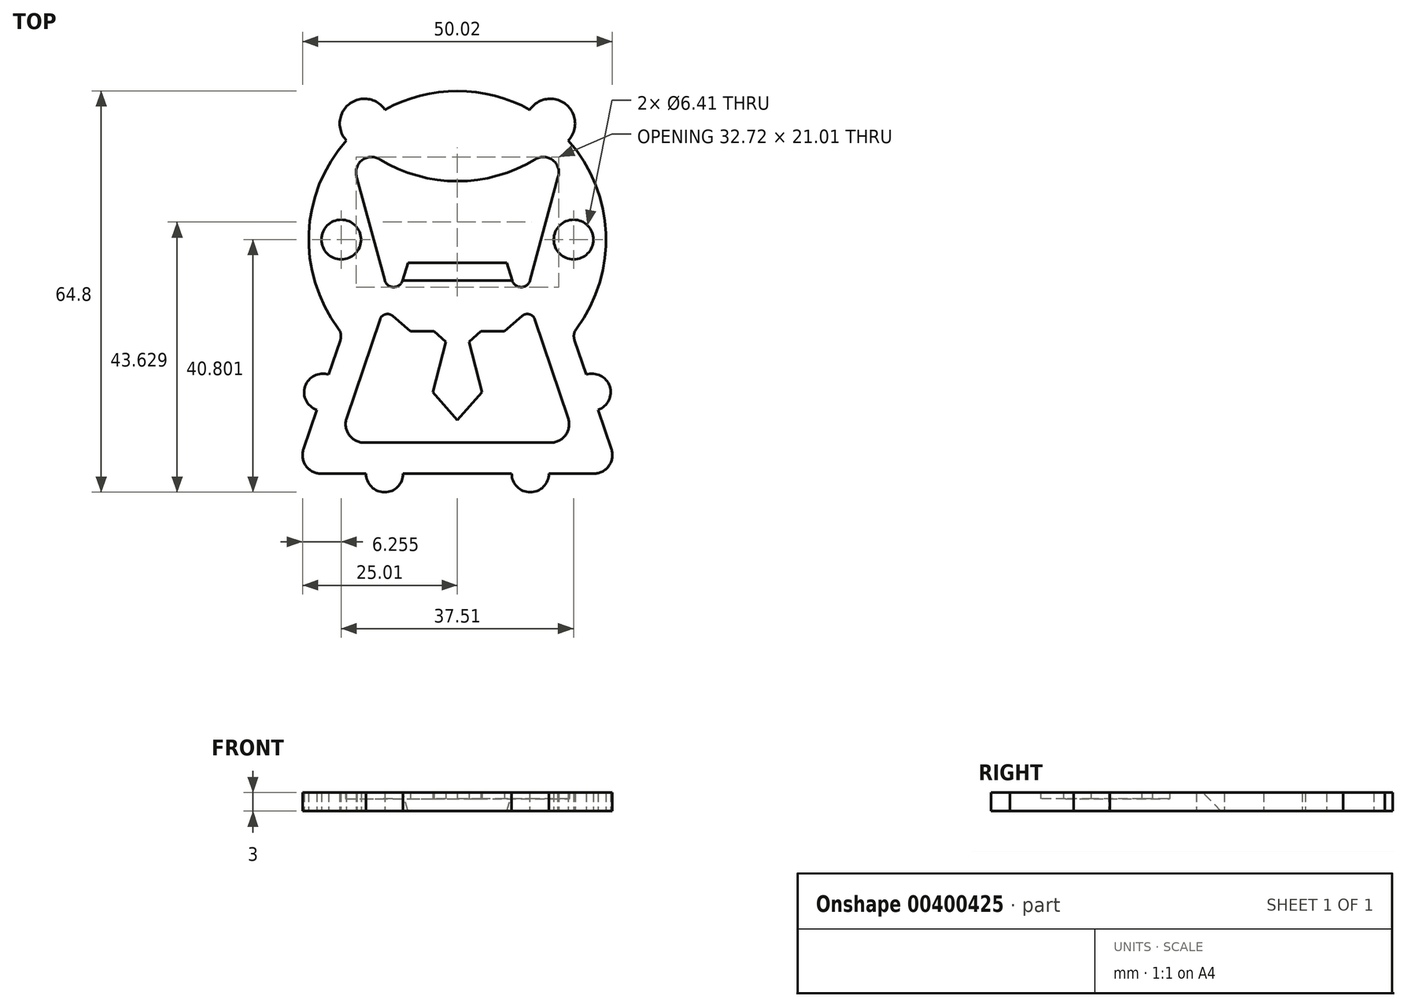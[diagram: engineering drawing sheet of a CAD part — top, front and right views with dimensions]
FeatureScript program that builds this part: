
annotation { "Feature Type Name" : "Feature", "Feature Type Description" : "" }
export const myFeature = defineFeature(function(context is Context, id is Id, definition is map)
    precondition{}
    {
        {
            var Q0;
            Q0=qCreatedBy(makeId("Top.planeOp"),FACE);
            var sketch = newSketch(context, id + "F0", { "sketchPlane" : qUnion([Q0])});
            skArc(sketch, "E0", {"start": v(-17.9, 15.98) * mm, "mid": v(-23.98, 1.02) * mm, "end": v(-19.2, -14.4) * mm});
            skLineSegment(sketch, "E1", {"start": v(0, 45.46) * mm, "end": v(0, -40.89) * mm, "construction": true});
            skArc(sketch, "E2", {"start": v(-11.68, 20.97) * mm, "mid": v(-17.5, 21.86) * mm, "end": v(-17.9, 15.98) * mm});
            skArc(sketch, "E3.MirrorC", {"start": v(11.68, 20.97) * mm, "mid": v(17.5, 21.86) * mm, "end": v(17.9, 15.98) * mm});
            skArc(sketch, "E4.trimOffspring", {"start": v(11.68, 20.97) * mm, "mid": v(0, 24) * mm, "end": v(-11.68, 20.97) * mm});
            skLineSegment(sketch, "E5", {"start": v(18.9, -16.24) * mm, "end": v(20.79, -21.82) * mm});
            skLineSegment(sketch, "E6.MirrorCS", {"start": v(-18.9, -16.24) * mm, "end": v(-20.79, -21.82) * mm});
            skLineSegment(sketch, "E7", {"start": v(-22, -37.8) * mm, "end": v(-14.76, -37.8) * mm});
            skArc(sketch, "E8.trimOffspring", {"start": v(19.2, -14.4) * mm, "mid": v(23.98, 1.02) * mm, "end": v(17.9, 15.98) * mm});
            skArc(sketch, "E9", {"start": v(-12.64, 13.03) * mm, "mid": v(-12.6, 13) * mm, "end": v(-12.56, 12.97) * mm});
            skCircle(sketch, "E10", {"center": v(-18.76, 0) * mm, "radius": 3.2 * mm});
            skCircle(sketch, "E11.MirrorC", {"center": v(18.76, 0) * mm, "radius": 3.2 * mm});
            skLineSegment(sketch, "E12.trimOffspring", {"start": v(-13.51, 0) * mm, "end": v(45.54, 0) * mm, "construction": true});
            skPoint(sketch, "E13.start.orphan", {"position": v(-42.84, 0) * mm});
            skPoint(sketch, "E14.orphan", {"position": v(-24, 0) * mm});
            skLineSegment(sketch, "E15", {"start": v(-13.51, 0) * mm, "end": v(-27.9, 0) * mm, "construction": true});
            skArc(sketch, "E16", {"start": v(22.7, -27.5) * mm, "mid": v(24.59, -23.7) * mm, "end": v(20.79, -21.82) * mm});
            skArc(sketch, "E17", {"start": v(8.76, -37.8) * mm, "mid": v(11.76, -40.8) * mm, "end": v(14.76, -37.8) * mm});
            skLineSegment(sketch, "E18.trimOffspring", {"start": v(14.76, -37.8) * mm, "end": v(22, -37.8) * mm});
            skLineSegment(sketch, "E19.trimOffspring", {"start": v(22.7, -27.5) * mm, "end": v(24.85, -33.84) * mm});
            skArc(sketch, "E20.MirrorCS", {"start": v(-22.7, -27.5) * mm, "mid": v(-24.59, -23.7) * mm, "end": v(-20.79, -21.82) * mm});
            skArc(sketch, "E21.MirrorCS", {"start": v(-8.76, -37.8) * mm, "mid": v(-11.76, -40.8) * mm, "end": v(-14.76, -37.8) * mm});
            skLineSegment(sketch, "E22.trimOffspring", {"start": v(-22.7, -27.5) * mm, "end": v(-24.85, -33.84) * mm});
            skLineSegment(sketch, "E23.trimOffspring", {"start": v(-8.76, -37.8) * mm, "end": v(8.76, -37.8) * mm});
            skLineSegment(sketch, "E24", {"start": v(-15.04, -32.8) * mm, "end": v(0, -32.8) * mm});
            skLineSegment(sketch, "E25", {"start": v(-17.88, -28.84) * mm, "end": v(-12.5, -12.89) * mm});
            skPoint(sketch, "E26.visualSharp", {"position": v(-19.22, -32.8) * mm});
            skArc(sketch, "E26.filletArc", {"start": v(-17.88, -28.84) * mm, "mid": v(-17.48, -31.55) * mm, "end": v(-15.04, -32.8) * mm});
            skPoint(sketch, "E27.visualSharp", {"position": v(-26.19, -37.8) * mm});
            skArc(sketch, "E27.filletArc", {"start": v(-24.85, -33.84) * mm, "mid": v(-24.45, -36.55) * mm, "end": v(-22, -37.8) * mm});
            skPoint(sketch, "E28.visualSharp", {"position": v(-18.56, -15.22) * mm});
            skArc(sketch, "E28.filletArc", {"start": v(-18.9, -16.24) * mm, "mid": v(-18.82, -15.29) * mm, "end": v(-19.2, -14.4) * mm});
            skPoint(sketch, "E29.visualSharp", {"position": v(18.56, -15.22) * mm});
            skArc(sketch, "E29.filletArc", {"start": v(19.2, -14.4) * mm, "mid": v(18.82, -15.29) * mm, "end": v(18.9, -16.24) * mm});
            skPoint(sketch, "E30.visualSharp", {"position": v(26.19, -37.8) * mm});
            skArc(sketch, "E30.filletArc", {"start": v(22, -37.8) * mm, "mid": v(24.45, -36.55) * mm, "end": v(24.85, -33.84) * mm});
            skPoint(sketch, "E31.visualSharp", {"position": v(-6.69, -6.62) * mm});
            skPoint(sketch, "E32.visualSharp", {"position": v(6.69, -6.62) * mm});
            skLineSegment(sketch, "E33", {"start": v(-10.46, -12.33) * mm, "end": v(-7.59, -14.8) * mm});
            skPoint(sketch, "E34.visualSharp", {"position": v(-11.9, -11.1) * mm});
            skArc(sketch, "E34.filletArc", {"start": v(-10.46, -12.33) * mm, "mid": v(-11.63, -12.07) * mm, "end": v(-12.5, -12.89) * mm});
            skLineSegment(sketch, "E35", {"start": v(-7.59, -14.8) * mm, "end": v(0, -14.8) * mm});
            skLineSegment(sketch, "E36", {"start": v(-3.8, -14.8) * mm, "end": v(0, -18.24) * mm});
            skLineSegment(sketch, "E37", {"start": v(-1.9, -16.52) * mm, "end": v(-3.98, -24.68) * mm});
            skLineSegment(sketch, "E38", {"start": v(-3.98, -24.68) * mm, "end": v(0, -29.16) * mm});
            skLineSegment(sketch, "E39.MirrorCS", {"start": v(7.59, -14.8) * mm, "end": v(0, -14.8) * mm});
            skLineSegment(sketch, "E40.MirrorCS", {"start": v(10.46, -12.33) * mm, "end": v(7.59, -14.8) * mm});
            skArc(sketch, "E41.MirrorCS", {"start": v(10.46, -12.33) * mm, "mid": v(11.63, -12.07) * mm, "end": v(12.5, -12.89) * mm});
            skLineSegment(sketch, "E42.MirrorCS", {"start": v(17.88, -28.84) * mm, "end": v(12.5, -12.89) * mm});
            skLineSegment(sketch, "E43.MirrorCS", {"start": v(15.04, -32.8) * mm, "end": v(0, -32.8) * mm});
            skArc(sketch, "E44.MirrorCS", {"start": v(17.88, -28.84) * mm, "mid": v(17.48, -31.55) * mm, "end": v(15.04, -32.8) * mm});
            skLineSegment(sketch, "E45.MirrorCS", {"start": v(3.98, -24.68) * mm, "end": v(0, -29.16) * mm});
            skLineSegment(sketch, "E46.MirrorCS", {"start": v(1.9, -16.52) * mm, "end": v(3.98, -24.68) * mm});
            skLineSegment(sketch, "E47.MirrorCS", {"start": v(3.8, -14.8) * mm, "end": v(0, -18.24) * mm});
            skPoint(sketch, "E48.MirrorCS.end.orphan", {"position": v(0, 9.42) * mm});
            skPoint(sketch, "E48.MirrorCS.start.orphan", {"position": v(12.64, 13.03) * mm});
            skPoint(sketch, "E49.orphan", {"position": v(16.19, 9.92) * mm});
            skPoint(sketch, "E50.MirrorCS.end.orphan", {"position": v(0, -6.62) * mm});
            skPoint(sketch, "E51.MirrorCS.start.orphan", {"position": v(11.72, -6.62) * mm});
            skArc(sketch, "E52.MirrorCS", {"start": v(12.64, 13.03) * mm, "mid": v(6.57, 10.34) * mm, "end": v(0, 9.42) * mm});
            skArc(sketch, "E53.MirrorCS", {"start": v(12.56, 12.97) * mm, "mid": v(15.48, 12.76) * mm, "end": v(16.19, 9.92) * mm});
            skLineSegment(sketch, "E54.MirrorCS", {"start": v(16.19, 9.92) * mm, "end": v(11.72, -6.62) * mm});
            skArc(sketch, "E55", {"start": v(8.85, -6.62) * mm, "mid": v(10.31, -7.68) * mm, "end": v(11.74, -6.57) * mm});
            skLineSegment(sketch, "E56", {"start": v(8.85, -6.62) * mm, "end": v(7.98, -3.75) * mm});
            skLineSegment(sketch, "E57", {"start": v(7.98, -3.75) * mm, "end": v(0, -3.75) * mm});
            skPoint(sketch, "E58.orphan", {"position": v(-16.19, 9.92) * mm});
            skPoint(sketch, "E59.center.orphan", {"position": v(-9.2, -6.62) * mm});
            skPoint(sketch, "E59.start.orphan", {"position": v(-11.72, -6.62) * mm});
            skArc(sketch, "E60.MirrorCS", {"start": v(-12.64, 13.03) * mm, "mid": v(-6.57, 10.34) * mm, "end": v(0, 9.42) * mm});
            skArc(sketch, "E61.MirrorCS", {"start": v(-12.56, 12.97) * mm, "mid": v(-15.48, 12.76) * mm, "end": v(-16.19, 9.92) * mm});
            skLineSegment(sketch, "E62.MirrorCS", {"start": v(-16.19, 9.92) * mm, "end": v(-11.72, -6.62) * mm});
            skArc(sketch, "E63.MirrorC", {"start": v(-8.85, -6.62) * mm, "mid": v(-10.31, -7.68) * mm, "end": v(-11.74, -6.57) * mm});
            skLineSegment(sketch, "E64.MirrorCS", {"start": v(-7.98, -3.75) * mm, "end": v(0, -3.75) * mm});
            skLineSegment(sketch, "E65.MirrorCS", {"start": v(-8.85, -6.62) * mm, "end": v(-7.98, -3.75) * mm});
            skLineSegment(sketch, "E66", {"start": v(8.85, -6.62) * mm, "end": v(-8.85, -6.62) * mm});
            skSolve(sketch);
        }
        {
            var Q0;
            Q0=makeQuery(id+"F0.imprint","IMPRINT",FACE,{"disambiguationData":[TD([[makeQuery(id+"F0.imprint","IMPRINT",EDGE,{"derivedFrom":sQuery(id+"F0.wireOp",EDGE,"E0")}),1.0]])]});
            var Q1;
            Q1=makeQuery(id+"F0.imprint","IMPRINT",FACE,{"disambiguationData":[TD([[makeQuery(id+"F0.imprint","IMPRINT",EDGE,{"derivedFrom":sQuery(id+"F0.wireOp",EDGE,"E24")}),1.0]])]});
            var Q2;
            {var subQ4=sQuery(id+"F0.wireOp",EDGE,"E37");Q2=makeQuery(id+"F0.imprint","IMPRINT",FACE,{"disambiguationData":[TD([[makeQuery(id+"F0.imprint","IMPRINT",EDGE,{"derivedFrom":subQ4}),1.0]])]});}
            var Q3;
            {var subQ4=sQuery(id+"F0.wireOp",EDGE,"E39.MirrorCS");var subQ5=sQuery(id+"F0.wireOp",EDGE,"E35");var subQ6=makeQuery(id+"F0.imprint","INTERSECT",VERTEX,{"derivedFrom":[subQ5,subQ4]});Q3=makeQuery(id+"F0.imprint","IMPRINT",FACE,{"disambiguationData":[TD([[makeQuery(id+"F0.imprint","IMPRINT",EDGE,{"disambiguationData":[TD([[subQ6,1.0]])],"derivedFrom":subQ5}),-1.0]])]});}
            var Q4;
            Q4=makeQuery(id+"F0.imprint","IMPRINT",FACE,{"disambiguationData":[TD([[makeQuery(id+"F0.imprint","IMPRINT",EDGE,{"derivedFrom":sQuery(id+"F0.wireOp",EDGE,"E56")}),1.0]])]});
            extrude(context, id + "F1", {"entities" : qUnion([Q0, Q1, Q2, Q3, Q4]), "depth" : 3 * mm});
        }
        {
            var Q0;
            Q0=makeQuery(id+"F0.imprint","IMPRINT",FACE,{"disambiguationData":[TD([[makeQuery(id+"F0.imprint","IMPRINT",EDGE,{"derivedFrom":sQuery(id+"F0.wireOp",EDGE,"E24")}),1.0]])]});
            extrude(context, id + "F2", {"entities" : qUnion([Q0]), "operationType" : NewBodyOperationType.REMOVE, "depth" : 25.4 * mm});
        }
        {
            var Q0;
            Q0=makeQuery(id+"F0.imprint","IMPRINT",FACE,{"disambiguationData":[TD([[makeQuery(id+"F0.imprint","IMPRINT",EDGE,{"derivedFrom":sQuery(id+"F0.wireOp",EDGE,"E24")}),1.0]])]});
            extrude(context, id + "F3", {"entities" : qUnion([Q0]), "operationType" : NewBodyOperationType.ADD, "depth" : 2 * mm});
        }
        {
            var Q0;
            Q0=qCreatedBy(makeId("Right.planeOp"),FACE);
            var sketch = newSketch(context, id + "F4", { "sketchPlane" : qUnion([Q0])});
            skLineSegment(sketch, "E67", {"start": v(-6.7, 3.08) * mm, "end": v(-3.71, 0) * mm});
            skLineSegment(sketch, "E68", {"start": v(-6.7, 3.08) * mm, "end": v(-3.72, 3.09) * mm});
            skLineSegment(sketch, "E69", {"start": v(-3.71, 0) * mm, "end": v(-3.72, 3.09) * mm});
            skSolve(sketch);
        }
        {
            var Q0;
            Q0 = qSketchRegion(id + "F4", true);
            extrude(context, id + "F5", {"entities" : qUnion([Q0]), "operationType" : NewBodyOperationType.REMOVE, "endBound" : BoundingType.SYMMETRIC, "oppositeDirection" : true, "depth" : 20 * mm});
        }
    });
